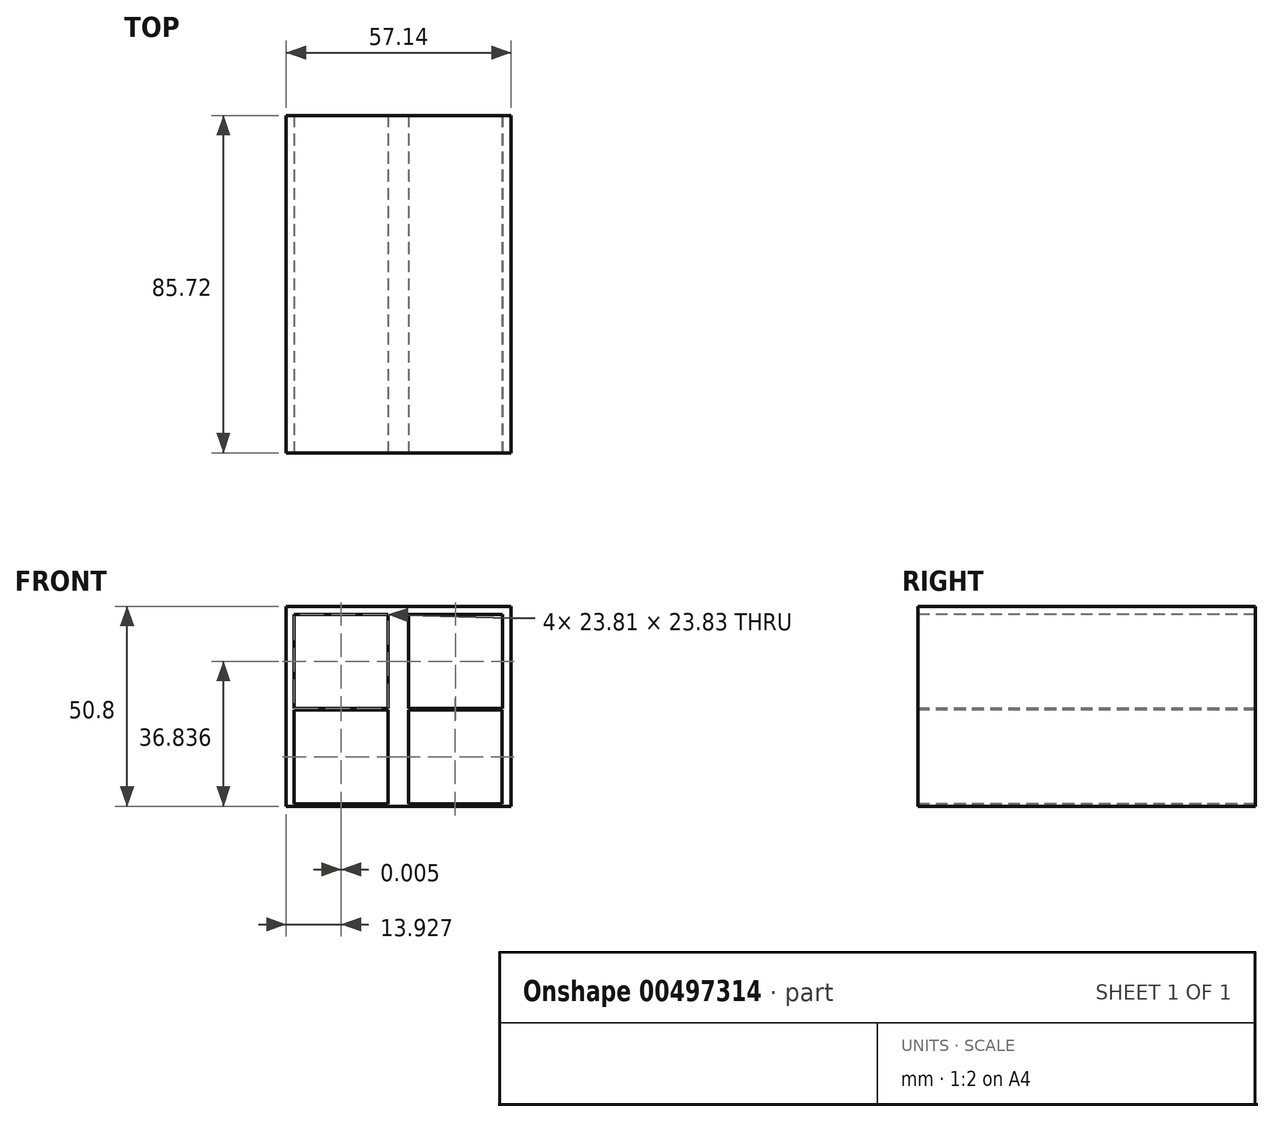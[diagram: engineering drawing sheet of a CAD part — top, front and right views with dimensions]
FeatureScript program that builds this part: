
annotation { "Feature Type Name" : "Feature", "Feature Type Description" : "" }
export const myFeature = defineFeature(function(context is Context, id is Id, definition is map)
    precondition{}
    {
        {
            var Q0;
            Q0=qCreatedBy(makeId("Front.planeOp"),FACE);
            var sketch = newSketch(context, id + "F0", { "sketchPlane" : qUnion([Q0])});
            skLineSegment(sketch, "E0.bottom", {"start": v(-28.58, 25.4) * mm, "end": v(28.58, 25.4) * mm});
            skLineSegment(sketch, "E0.top", {"start": v(-28.58, -25.4) * mm, "end": v(28.58, -25.4) * mm});
            skLineSegment(sketch, "E0.left", {"start": v(-28.58, 25.4) * mm, "end": v(-28.58, -25.4) * mm});
            skLineSegment(sketch, "E0.right", {"start": v(28.58, 25.4) * mm, "end": v(28.58, -25.4) * mm});
            skPoint(sketch, "E0.middle", {"position": v(0, 0) * mm});
            skSolve(sketch);
        }
        {
            var Q0;
            Q0=makeQuery(id+"F0.imprint","IMPRINT",FACE,{"disambiguationData":[TD([[makeQuery(id+"F0.imprint","IMPRINT",EDGE,{"derivedFrom":sQuery(id+"F0.wireOp",EDGE,"E0.bottom")}),-1.0]])]});
            extrude(context, id + "F1", {"entities" : qUnion([Q0]), "depth" : 85.72 * mm});
        }
        {
            var Q0;
            Q0=makeQuery(id+"F1.opExtrude","CAP_FACE",FACE,{"disambiguationData":[OSD([sQuery(id+"F0.wireOp",EDGE,"E0.bottom"),sQuery(id+"F0.wireOp",EDGE,"E0.top"),sQuery(id+"F0.wireOp",EDGE,"E0.left"),sQuery(id+"F0.wireOp",EDGE,"E0.right")])],"isStart":false});
            var sketch = newSketch(context, id + "F2", { "sketchPlane" : qUnion([Q0])});
            skLineSegment(sketch, "E1.bottom", {"start": v(-26.55, 23.35) * mm, "end": v(-2.74, 23.35) * mm});
            skLineSegment(sketch, "E1.top", {"start": v(-26.55, -0.48) * mm, "end": v(-2.74, -0.48) * mm});
            skLineSegment(sketch, "E1.left", {"start": v(-26.55, 23.35) * mm, "end": v(-26.55, -0.48) * mm});
            skLineSegment(sketch, "E1.right", {"start": v(-2.74, 23.35) * mm, "end": v(-2.74, -0.48) * mm});
            skPoint(sketch, "E1.middle", {"position": v(-14.64, 11.44) * mm});
            skSolve(sketch);
        }
        {
            var Q0;
            Q0 = qSketchRegion(id + "F2", true);
            extrude(context, id + "F3", {"entities" : qUnion([Q0]), "operationType" : NewBodyOperationType.REMOVE, "endBound" : BoundingType.THROUGH_ALL, "oppositeDirection" : true, "depth" : 25.4 * mm});
        }
        {
            var Q0;
            Q0=makeQuery(id+"F1.opExtrude","CAP_FACE",FACE,{"disambiguationData":[OSD([sQuery(id+"F0.wireOp",EDGE,"E0.bottom"),sQuery(id+"F0.wireOp",EDGE,"E0.top"),sQuery(id+"F0.wireOp",EDGE,"E0.left"),sQuery(id+"F0.wireOp",EDGE,"E0.right")])],"isStart":false});
            var sketch = newSketch(context, id + "F4", { "sketchPlane" : qUnion([Q0])});
            skLineSegment(sketch, "E2.bottom", {"start": v(2.53, 23.34) * mm, "end": v(26.34, 23.34) * mm});
            skLineSegment(sketch, "E2.top", {"start": v(2.53, -0.48) * mm, "end": v(26.34, -0.48) * mm});
            skLineSegment(sketch, "E2.left", {"start": v(2.53, 23.34) * mm, "end": v(2.53, -0.48) * mm});
            skLineSegment(sketch, "E2.right", {"start": v(26.34, 23.34) * mm, "end": v(26.34, -0.48) * mm});
            skPoint(sketch, "E2.middle", {"position": v(14.44, 11.43) * mm});
            skSolve(sketch);
        }
        {
            var Q0;
            Q0 = qSketchRegion(id + "F4", true);
            extrude(context, id + "F5", {"entities" : qUnion([Q0]), "operationType" : NewBodyOperationType.REMOVE, "endBound" : BoundingType.THROUGH_ALL, "oppositeDirection" : true, "depth" : 25.4 * mm});
        }
        {
            var Q0;
            Q0=makeQuery(id+"F1.opExtrude","CAP_FACE",FACE,{"disambiguationData":[OSD([sQuery(id+"F0.wireOp",EDGE,"E0.bottom"),sQuery(id+"F0.wireOp",EDGE,"E0.top"),sQuery(id+"F0.wireOp",EDGE,"E0.left"),sQuery(id+"F0.wireOp",EDGE,"E0.right")])],"isStart":false});
            var sketch = newSketch(context, id + "F6", { "sketchPlane" : qUnion([Q0])});
            skLineSegment(sketch, "E3.bottom", {"start": v(-26.54, -0.92) * mm, "end": v(-2.73, -0.92) * mm});
            skLineSegment(sketch, "E3.top", {"start": v(-26.54, -24.75) * mm, "end": v(-2.73, -24.75) * mm});
            skLineSegment(sketch, "E3.left", {"start": v(-26.54, -0.92) * mm, "end": v(-26.54, -24.75) * mm});
            skLineSegment(sketch, "E3.right", {"start": v(-2.73, -0.92) * mm, "end": v(-2.73, -24.75) * mm});
            skPoint(sketch, "E3.middle", {"position": v(-14.64, -12.83) * mm});
            skSolve(sketch);
        }
        {
            var Q0;
            Q0 = qSketchRegion(id + "F6", true);
            extrude(context, id + "F7", {"entities" : qUnion([Q0]), "operationType" : NewBodyOperationType.REMOVE, "endBound" : BoundingType.THROUGH_ALL, "oppositeDirection" : true, "depth" : 25.4 * mm});
        }
        {
            var Q0;
            Q0=makeQuery(id+"F1.opExtrude","CAP_FACE",FACE,{"disambiguationData":[OSD([sQuery(id+"F0.wireOp",EDGE,"E0.bottom"),sQuery(id+"F0.wireOp",EDGE,"E0.top"),sQuery(id+"F0.wireOp",EDGE,"E0.left"),sQuery(id+"F0.wireOp",EDGE,"E0.right")])],"isStart":false});
            var sketch = newSketch(context, id + "F8", { "sketchPlane" : qUnion([Q0])});
            skLineSegment(sketch, "E4.bottom", {"start": v(2.43, -0.92) * mm, "end": v(26.24, -0.92) * mm});
            skLineSegment(sketch, "E4.top", {"start": v(2.43, -24.75) * mm, "end": v(26.24, -24.75) * mm});
            skLineSegment(sketch, "E4.left", {"start": v(2.43, -0.92) * mm, "end": v(2.43, -24.75) * mm});
            skLineSegment(sketch, "E4.right", {"start": v(26.24, -0.92) * mm, "end": v(26.24, -24.75) * mm});
            skPoint(sketch, "E4.middle", {"position": v(14.34, -12.83) * mm});
            skSolve(sketch);
        }
        {
            var Q0;
            Q0 = qSketchRegion(id + "F8", true);
            extrude(context, id + "F9", {"entities" : qUnion([Q0]), "operationType" : NewBodyOperationType.REMOVE, "endBound" : BoundingType.THROUGH_ALL, "oppositeDirection" : true, "depth" : 25.4 * mm});
        }
    });
